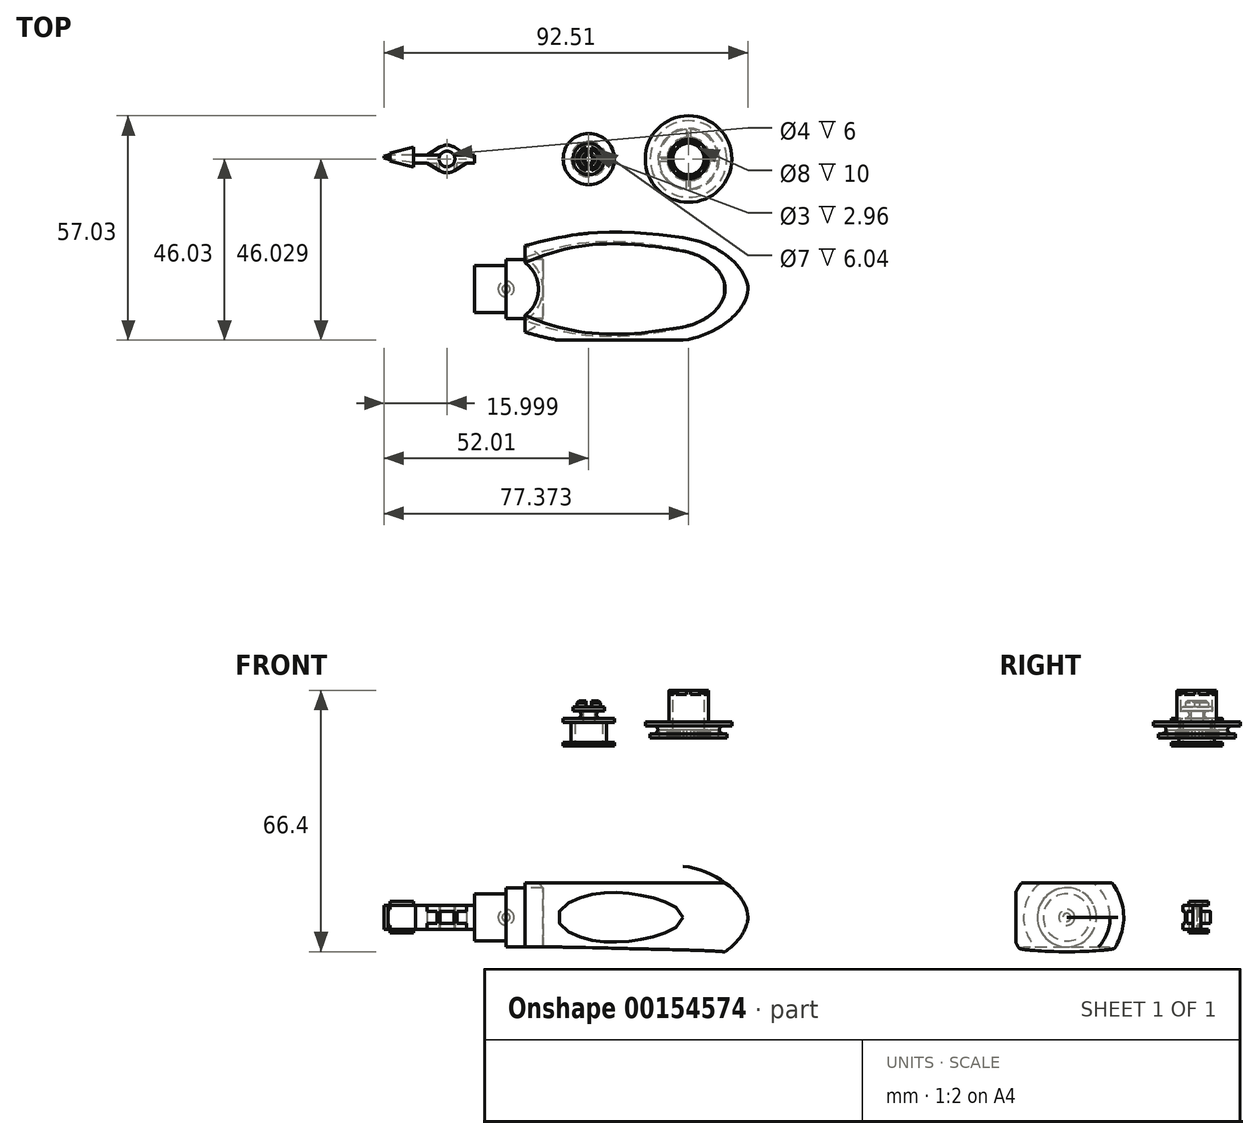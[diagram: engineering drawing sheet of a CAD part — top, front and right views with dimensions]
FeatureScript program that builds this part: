
annotation { "Feature Type Name" : "Feature", "Feature Type Description" : "" }
export const myFeature = defineFeature(function(context is Context, id is Id, definition is map)
    precondition{}
    {
        {
            var Q0;
            Q0=qCreatedBy(makeId("Front.planeOp"),FACE);
            var sketch = newSketch(context, id + "F0", { "sketchPlane" : qUnion([Q0])});
            skLineSegment(sketch, "E0", {"start": v(0, 53.5) * mm, "end": v(1, 53.5) * mm});
            skLineSegment(sketch, "E1", {"start": v(1, 53.5) * mm, "end": v(1, 54.5) * mm});
            skLineSegment(sketch, "E2", {"start": v(1.5, 55) * mm, "end": v(2.5, 55) * mm});
            skLineSegment(sketch, "E3", {"start": v(3, 54.5) * mm, "end": v(3, 53.5) * mm});
            skLineSegment(sketch, "E4", {"start": v(3, 53.5) * mm, "end": v(4, 53.5) * mm});
            skLineSegment(sketch, "E5", {"start": v(4, 53.5) * mm, "end": v(4, 52.5) * mm});
            skLineSegment(sketch, "E6", {"start": v(4, 52.5) * mm, "end": v(3, 52.5) * mm});
            skLineSegment(sketch, "E7", {"start": v(0, 52.5) * mm, "end": v(0, 53.5) * mm});
            skLineSegment(sketch, "E8", {"start": v(3, 50.5) * mm, "end": v(6.5, 50.5) * mm});
            skLineSegment(sketch, "E9", {"start": v(6.5, 50.5) * mm, "end": v(6.5, 49.54) * mm});
            skLineSegment(sketch, "E10", {"start": v(6.5, 49.54) * mm, "end": v(4.5, 49.54) * mm});
            skLineSegment(sketch, "E11", {"start": v(4.5, 49.54) * mm, "end": v(4.5, 44.5) * mm});
            skLineSegment(sketch, "E12", {"start": v(4.5, 44.5) * mm, "end": v(6.5, 44.5) * mm});
            skLineSegment(sketch, "E13", {"start": v(6.5, 44.5) * mm, "end": v(6.5, 43.5) * mm});
            skLineSegment(sketch, "E14", {"start": v(6.5, 43.5) * mm, "end": v(3.5, 43.5) * mm});
            skLineSegment(sketch, "E15", {"start": v(3.5, 43.5) * mm, "end": v(3.5, 49.54) * mm});
            skLineSegment(sketch, "E16", {"start": v(1.5, 52.5) * mm, "end": v(0, 52.5) * mm});
            skArc(sketch, "E17", {"start": v(3, 52.5) * mm, "mid": v(2, 51.5) * mm, "end": v(3, 50.5) * mm});
            skLineSegment(sketch, "E18", {"start": v(1.5, 52.5) * mm, "end": v(1.5, 49.54) * mm});
            skLineSegment(sketch, "E19", {"start": v(1.5, 49.54) * mm, "end": v(3.5, 49.54) * mm});
            skLineSegment(sketch, "E20", {"start": v(1, 54.5) * mm, "end": v(1.5, 55) * mm});
            skLineSegment(sketch, "E21", {"start": v(2.5, 55) * mm, "end": v(3, 54.5) * mm});
            skLineSegment(sketch, "E22", {"start": v(0, 52.5) * mm, "end": v(0, 82.14) * mm, "construction": true});
            skSolve(sketch);
        }
        {
            var Q0;
            Q0 = qSketchRegion(id + "F0", true);
            var Q1;
            Q1=sQuery(id+"F0.wireOp",EDGE,"E22");
            revolve(context, id + "F1", {"entities" : qUnion([Q0]), "axis" : qUnion([Q1]), "revolveType" : RevolveType.FULL});
        }
        {
            var Q0;
            Q0=qCreatedBy(makeId("Front.planeOp"),FACE);
            var sketch = newSketch(context, id + "F2", { "sketchPlane" : qUnion([Q0])});
            skLineSegment(sketch, "E23", {"start": v(0, 53.5) * mm, "end": v(0.75, 53.5) * mm});
            skLineSegment(sketch, "E24", {"start": v(0.75, 53.5) * mm, "end": v(0.75, 55.5) * mm});
            skLineSegment(sketch, "E25", {"start": v(0.75, 55.5) * mm, "end": v(-0.75, 55.5) * mm});
            skLineSegment(sketch, "E26", {"start": v(-0.75, 55.5) * mm, "end": v(-0.75, 53.5) * mm});
            skLineSegment(sketch, "E27", {"start": v(-0.75, 53.5) * mm, "end": v(0, 53.5) * mm});
            skSolve(sketch);
        }
        {
            var Q0;
            Q0 = qSketchRegion(id + "F2", true);
            extrude(context, id + "F3", {"entities" : qUnion([Q0]), "operationType" : NewBodyOperationType.REMOVE, "endBound" : BoundingType.SYMMETRIC, "oppositeDirection" : true, "depth" : 25 * mm});
        }
        {
            var Q0;
            Q0=qCreatedBy(makeId("Front.planeOp"),FACE);
            var sketch = newSketch(context, id + "F4", { "sketchPlane" : qUnion([Q0])});
            skLineSegment(sketch, "E28", {"start": v(25.36, 78.8) * mm, "end": v(25.36, 27.62) * mm, "construction": true});
            skLineSegment(sketch, "E29", {"start": v(29.36, 57.64) * mm, "end": v(30.36, 57.64) * mm});
            skLineSegment(sketch, "E30", {"start": v(30.36, 57.64) * mm, "end": v(30.36, 49.64) * mm});
            skLineSegment(sketch, "E31", {"start": v(30.36, 49.64) * mm, "end": v(36.36, 49.64) * mm});
            skLineSegment(sketch, "E32", {"start": v(36.36, 49.64) * mm, "end": v(36.36, 48.64) * mm});
            skLineSegment(sketch, "E33", {"start": v(36.36, 48.64) * mm, "end": v(34.18, 48.64) * mm});
            skLineSegment(sketch, "E34", {"start": v(34.18, 46.64) * mm, "end": v(35.1, 46.64) * mm});
            skLineSegment(sketch, "E35", {"start": v(35.1, 46.64) * mm, "end": v(35.1, 45.64) * mm});
            skLineSegment(sketch, "E36", {"start": v(35.1, 45.64) * mm, "end": v(29.36, 45.64) * mm});
            skArc(sketch, "E37", {"start": v(34.18, 48.64) * mm, "mid": v(33.18, 47.64) * mm, "end": v(34.18, 46.64) * mm});
            skLineSegment(sketch, "E38", {"start": v(29.36, 57.64) * mm, "end": v(29.36, 45.64) * mm});
            skSolve(sketch);
        }
        {
            var Q0;
            Q0=makeQuery(id+"F4.imprint","IMPRINT",FACE,{"disambiguationData":[TD([[makeQuery(id+"F4.imprint","IMPRINT",EDGE,{"derivedFrom":sQuery(id+"F4.wireOp",EDGE,"E29")}),-1.0]])]});
            var Q1;
            Q1=sQuery(id+"F4.wireOp",EDGE,"E28");
            revolve(context, id + "F5", {"entities" : qUnion([Q0]), "axis" : qUnion([Q1]), "revolveType" : RevolveType.FULL});
        }
        {
            var Q0;
            Q0=makeQuery(id+"F5.opRevolve","SWEPT_FACE",FACE,{"disambiguationData":[OSD([sQuery(id+"F4.wireOp",EDGE,"E36")])]});
            var sketch = newSketch(context, id + "F6", { "sketchPlane" : qUnion([Q0])});
            skArc(sketch, "E39", {"start": v(23.92, 4.79) * mm, "mid": v(23.45, 4.62) * mm, "end": v(23, 4.4) * mm});
            skArc(sketch, "E40", {"start": v(24.86, 5.48) * mm, "mid": v(21.47, 3.89) * mm, "end": v(19.89, 0.5) * mm});
            skArc(sketch, "E41", {"start": v(24.86, 7.48) * mm, "mid": v(20.06, 5.3) * mm, "end": v(17.88, 0.5) * mm});
            skLineSegment(sketch, "E42", {"start": v(17.88, 0.5) * mm, "end": v(19.89, 0.5) * mm});
            skLineSegment(sketch, "E43.MirrorCS", {"start": v(17.88, -0.5) * mm, "end": v(19.89, -0.5) * mm});
            skLineSegment(sketch, "E44", {"start": v(25.36, 0) * mm, "end": v(25.36, 17.53) * mm, "construction": true});
            skLineSegment(sketch, "E45.MirrorCS", {"start": v(32.85, 0.5) * mm, "end": v(30.84, 0.5) * mm});
            skLineSegment(sketch, "E46.MirrorCS", {"start": v(32.85, -0.5) * mm, "end": v(30.84, -0.5) * mm});
            skLineSegment(sketch, "E47", {"start": v(24.86, 7.48) * mm, "end": v(24.86, 5.48) * mm});
            skLineSegment(sketch, "E48.MirrorCS", {"start": v(25.86, 7.48) * mm, "end": v(25.86, 5.48) * mm});
            skLineSegment(sketch, "E49.MirrorCS", {"start": v(24.86, -7.48) * mm, "end": v(24.86, -5.48) * mm});
            skLineSegment(sketch, "E50.MirrorCS", {"start": v(25.86, -7.48) * mm, "end": v(25.86, -5.48) * mm});
            skArc(sketch, "E51.trimOffspring", {"start": v(17.88, -0.5) * mm, "mid": v(20.06, -5.3) * mm, "end": v(24.86, -7.48) * mm});
            skArc(sketch, "E52.trimOffspring", {"start": v(19.89, -0.5) * mm, "mid": v(21.47, -3.89) * mm, "end": v(24.86, -5.48) * mm});
            skArc(sketch, "E53.trimOffspring", {"start": v(25.86, -5.48) * mm, "mid": v(29.25, -3.89) * mm, "end": v(30.84, -0.5) * mm});
            skArc(sketch, "E54.trimOffspring", {"start": v(25.86, -7.48) * mm, "mid": v(30.67, -5.3) * mm, "end": v(32.85, -0.5) * mm});
            skArc(sketch, "E55.trimOffspring", {"start": v(30.84, 0.5) * mm, "mid": v(29.25, 3.89) * mm, "end": v(25.86, 5.48) * mm});
            skArc(sketch, "E56.trimOffspring", {"start": v(32.85, 0.5) * mm, "mid": v(30.67, 5.3) * mm, "end": v(25.86, 7.48) * mm});
            skLineSegment(sketch, "E57", {"start": v(24.86, 4.97) * mm, "end": v(24.86, 4.47) * mm});
            skArc(sketch, "E58", {"start": v(24.86, 4.47) * mm, "mid": v(24.48, 4.41) * mm, "end": v(24.11, 4.32) * mm});
            skLineSegment(sketch, "E59.MirrorCS", {"start": v(25.86, 4.97) * mm, "end": v(25.86, 4.47) * mm});
            skLineSegment(sketch, "E60.1.0", {"start": v(23, 4.4) * mm, "end": v(23.19, 3.94) * mm});
            skLineSegment(sketch, "E60.1.1", {"start": v(23.92, 4.79) * mm, "end": v(24.11, 4.32) * mm});
            skLineSegment(sketch, "E60.2.0", {"start": v(21.5, 3.16) * mm, "end": v(21.85, 2.8) * mm});
            skLineSegment(sketch, "E60.2.1", {"start": v(22.2, 3.87) * mm, "end": v(22.55, 3.52) * mm});
            skLineSegment(sketch, "E60.3.0", {"start": v(20.57, 1.44) * mm, "end": v(21.04, 1.25) * mm});
            skLineSegment(sketch, "E60.3.1", {"start": v(20.96, 2.37) * mm, "end": v(21.42, 2.17) * mm});
            skLineSegment(sketch, "E60.4.0", {"start": v(20.39, -0.5) * mm, "end": v(20.9, -0.5) * mm});
            skLineSegment(sketch, "E60.4.1", {"start": v(20.39, 0.5) * mm, "end": v(20.9, 0.5) * mm});
            skLineSegment(sketch, "E60.5.0", {"start": v(20.96, -2.37) * mm, "end": v(21.42, -2.17) * mm});
            skLineSegment(sketch, "E60.5.1", {"start": v(20.57, -1.44) * mm, "end": v(21.04, -1.25) * mm});
            skLineSegment(sketch, "E60.6.0", {"start": v(22.2, -3.87) * mm, "end": v(22.55, -3.52) * mm});
            skLineSegment(sketch, "E60.6.1", {"start": v(21.5, -3.16) * mm, "end": v(21.85, -2.8) * mm});
            skLineSegment(sketch, "E60.7.0", {"start": v(23.92, -4.79) * mm, "end": v(24.11, -4.32) * mm});
            skLineSegment(sketch, "E60.7.1", {"start": v(23, -4.4) * mm, "end": v(23.19, -3.94) * mm});
            skLineSegment(sketch, "E60.8.0", {"start": v(25.86, -4.97) * mm, "end": v(25.86, -4.47) * mm});
            skLineSegment(sketch, "E60.8.1", {"start": v(24.86, -4.97) * mm, "end": v(24.86, -4.47) * mm});
            skLineSegment(sketch, "E60.9.0", {"start": v(27.73, -4.4) * mm, "end": v(27.54, -3.94) * mm});
            skLineSegment(sketch, "E60.9.1", {"start": v(26.8, -4.79) * mm, "end": v(26.61, -4.32) * mm});
            skLineSegment(sketch, "E60.10.0", {"start": v(29.23, -3.16) * mm, "end": v(28.88, -2.8) * mm});
            skLineSegment(sketch, "E60.10.1", {"start": v(28.53, -3.87) * mm, "end": v(28.17, -3.52) * mm});
            skLineSegment(sketch, "E60.11.0", {"start": v(30.15, -1.44) * mm, "end": v(29.69, -1.25) * mm});
            skLineSegment(sketch, "E60.11.1", {"start": v(29.77, -2.37) * mm, "end": v(29.3, -2.17) * mm});
            skLineSegment(sketch, "E60.12.0", {"start": v(30.34, 0.5) * mm, "end": v(29.83, 0.5) * mm});
            skLineSegment(sketch, "E60.12.1", {"start": v(30.34, -0.5) * mm, "end": v(29.83, -0.5) * mm});
            skLineSegment(sketch, "E60.13.0", {"start": v(29.77, 2.37) * mm, "end": v(29.3, 2.17) * mm});
            skLineSegment(sketch, "E60.13.1", {"start": v(30.15, 1.44) * mm, "end": v(29.69, 1.25) * mm});
            skLineSegment(sketch, "E60.14.0", {"start": v(28.53, 3.87) * mm, "end": v(28.17, 3.52) * mm});
            skLineSegment(sketch, "E60.14.1", {"start": v(29.23, 3.16) * mm, "end": v(28.88, 2.8) * mm});
            skLineSegment(sketch, "E60.15.0", {"start": v(26.8, 4.79) * mm, "end": v(26.61, 4.32) * mm});
            skLineSegment(sketch, "E60.15.1", {"start": v(27.73, 4.4) * mm, "end": v(27.54, 3.94) * mm});
            skArc(sketch, "E61.trimOffspring", {"start": v(26.61, 4.32) * mm, "mid": v(26.24, 4.41) * mm, "end": v(25.86, 4.47) * mm});
            skArc(sketch, "E62.trimOffspring", {"start": v(28.17, 3.52) * mm, "mid": v(27.86, 3.74) * mm, "end": v(27.54, 3.94) * mm});
            skArc(sketch, "E63.trimOffspring", {"start": v(29.3, 2.17) * mm, "mid": v(29.1, 2.5) * mm, "end": v(28.88, 2.8) * mm});
            skArc(sketch, "E64.trimOffspring", {"start": v(29.83, 0.5) * mm, "mid": v(29.78, 0.88) * mm, "end": v(29.69, 1.25) * mm});
            skArc(sketch, "E65.trimOffspring", {"start": v(29.69, -1.25) * mm, "mid": v(29.78, -0.88) * mm, "end": v(29.83, -0.5) * mm});
            skArc(sketch, "E66.trimOffspring", {"start": v(28.88, -2.8) * mm, "mid": v(29.1, -2.5) * mm, "end": v(29.3, -2.17) * mm});
            skArc(sketch, "E67.trimOffspring", {"start": v(27.54, -3.94) * mm, "mid": v(27.86, -3.74) * mm, "end": v(28.17, -3.52) * mm});
            skArc(sketch, "E68.trimOffspring", {"start": v(25.86, -4.47) * mm, "mid": v(26.24, -4.41) * mm, "end": v(26.61, -4.32) * mm});
            skArc(sketch, "E69.trimOffspring", {"start": v(24.11, -4.32) * mm, "mid": v(24.48, -4.41) * mm, "end": v(24.86, -4.47) * mm});
            skArc(sketch, "E70.trimOffspring", {"start": v(22.55, -3.52) * mm, "mid": v(22.86, -3.74) * mm, "end": v(23.19, -3.94) * mm});
            skArc(sketch, "E71.trimOffspring", {"start": v(21.42, -2.17) * mm, "mid": v(21.62, -2.5) * mm, "end": v(21.85, -2.8) * mm});
            skArc(sketch, "E72.trimOffspring", {"start": v(20.9, -0.5) * mm, "mid": v(20.95, -0.88) * mm, "end": v(21.04, -1.25) * mm});
            skArc(sketch, "E73.trimOffspring", {"start": v(21.04, 1.25) * mm, "mid": v(20.95, 0.88) * mm, "end": v(20.9, 0.5) * mm});
            skArc(sketch, "E74.trimOffspring", {"start": v(21.85, 2.8) * mm, "mid": v(21.62, 2.5) * mm, "end": v(21.42, 2.17) * mm});
            skArc(sketch, "E75.trimOffspring", {"start": v(23.19, 3.94) * mm, "mid": v(22.86, 3.74) * mm, "end": v(22.55, 3.52) * mm});
            skArc(sketch, "E76.trimOffspring", {"start": v(25.86, 4.97) * mm, "mid": v(25.36, 5) * mm, "end": v(24.86, 4.97) * mm});
            skArc(sketch, "E77.trimOffspring", {"start": v(27.73, 4.4) * mm, "mid": v(27.28, 4.62) * mm, "end": v(26.8, 4.79) * mm});
            skArc(sketch, "E78.trimOffspring", {"start": v(29.23, 3.16) * mm, "mid": v(28.9, 3.54) * mm, "end": v(28.53, 3.87) * mm});
            skArc(sketch, "E79.trimOffspring", {"start": v(30.15, 1.44) * mm, "mid": v(29.98, 1.91) * mm, "end": v(29.77, 2.37) * mm});
            skArc(sketch, "E80.trimOffspring", {"start": v(30.34, -0.5) * mm, "mid": v(30.36, 0) * mm, "end": v(30.34, 0.5) * mm});
            skArc(sketch, "E81.trimOffspring", {"start": v(29.77, -2.37) * mm, "mid": v(29.98, -1.91) * mm, "end": v(30.15, -1.44) * mm});
            skArc(sketch, "E82.trimOffspring", {"start": v(28.53, -3.87) * mm, "mid": v(28.9, -3.54) * mm, "end": v(29.23, -3.16) * mm});
            skArc(sketch, "E83.trimOffspring", {"start": v(26.8, -4.79) * mm, "mid": v(27.28, -4.62) * mm, "end": v(27.73, -4.4) * mm});
            skArc(sketch, "E84.trimOffspring", {"start": v(24.86, -4.97) * mm, "mid": v(25.36, -5) * mm, "end": v(25.86, -4.97) * mm});
            skArc(sketch, "E85.trimOffspring", {"start": v(23, -4.4) * mm, "mid": v(23.45, -4.62) * mm, "end": v(23.92, -4.79) * mm});
            skArc(sketch, "E86.trimOffspring", {"start": v(21.5, -3.16) * mm, "mid": v(21.83, -3.54) * mm, "end": v(22.2, -3.87) * mm});
            skArc(sketch, "E87.trimOffspring", {"start": v(20.57, -1.44) * mm, "mid": v(20.74, -1.91) * mm, "end": v(20.96, -2.37) * mm});
            skArc(sketch, "E88.trimOffspring", {"start": v(20.39, 0.5) * mm, "mid": v(20.36, 0) * mm, "end": v(20.39, -0.5) * mm});
            skArc(sketch, "E89.trimOffspring", {"start": v(20.96, 2.37) * mm, "mid": v(20.74, 1.91) * mm, "end": v(20.57, 1.44) * mm});
            skArc(sketch, "E90.trimOffspring", {"start": v(22.2, 3.87) * mm, "mid": v(21.83, 3.54) * mm, "end": v(21.5, 3.16) * mm});
            skSolve(sketch);
        }
        {
            var Q0;
            Q0=makeQuery(id+"F6.imprint","IMPRINT",FACE,{"disambiguationData":[TD([[makeQuery(id+"F6.imprint","IMPRINT",EDGE,{"derivedFrom":sQuery(id+"F6.wireOp",EDGE,"E40")}),-1.0]])]});
            var Q1;
            Q1=makeQuery(id+"F6.imprint","IMPRINT",FACE,{"disambiguationData":[TD([[makeQuery(id+"F6.imprint","IMPRINT",EDGE,{"derivedFrom":sQuery(id+"F6.wireOp",EDGE,"E45.MirrorCS")}),-1.0]])]});
            var Q2;
            Q2=makeQuery(id+"F6.imprint","IMPRINT",FACE,{"disambiguationData":[TD([[makeQuery(id+"F6.imprint","IMPRINT",EDGE,{"derivedFrom":sQuery(id+"F6.wireOp",EDGE,"E46.MirrorCS")}),1.0]])]});
            var Q3;
            Q3=makeQuery(id+"F6.imprint","IMPRINT",FACE,{"disambiguationData":[TD([[makeQuery(id+"F6.imprint","IMPRINT",EDGE,{"derivedFrom":sQuery(id+"F6.wireOp",EDGE,"E43.MirrorCS")}),-1.0]])]});
            var Q4;
            Q4=makeQuery(id+"F6.imprint","IMPRINT",FACE,{"disambiguationData":[TD([[makeQuery(id+"F6.imprint","IMPRINT",EDGE,{"derivedFrom":sQuery(id+"F6.wireOp",EDGE,"E39")}),1.0]])]});
            extrude(context, id + "F7", {"entities" : qUnion([Q0, Q1, Q2, Q3, Q4]), "operationType" : NewBodyOperationType.REMOVE, "oppositeDirection" : true, "depth" : 2 * mm});
        }
        {
            var Q0;
            Q0=makeQuery(id+"F5.opRevolve","SWEPT_FACE",FACE,{"disambiguationData":[OSD([sQuery(id+"F4.wireOp",EDGE,"E29")])]});
            var sketch = newSketch(context, id + "F8", { "sketchPlane" : qUnion([Q0])});
            skArc(sketch, "E91", {"start": v(24.86, 4.47) * mm, "mid": v(23.64, 4.16) * mm, "end": v(22.55, 3.52) * mm});
            skLineSegment(sketch, "E92", {"start": v(25.36, 0) * mm, "end": v(25.36, 7.06) * mm, "construction": true});
            skLineSegment(sketch, "E93", {"start": v(24.86, 4.97) * mm, "end": v(24.86, 4.47) * mm});
            skArc(sketch, "E94", {"start": v(25.86, 4.97) * mm, "mid": v(25.36, 5) * mm, "end": v(24.86, 4.97) * mm});
            skLineSegment(sketch, "E95.MirrorCS", {"start": v(25.86, 4.97) * mm, "end": v(25.86, 4.47) * mm});
            skLineSegment(sketch, "E96.1.0", {"start": v(-16.74, 19.04) * mm, "end": v(-16.3, 19.3) * mm});
            skArc(sketch, "E96.1.1", {"start": v(-17.24, 19.91) * mm, "mid": v(-17.01, 19.46) * mm, "end": v(-16.74, 19.04) * mm});
            skLineSegment(sketch, "E96.1.2", {"start": v(-17.24, 19.91) * mm, "end": v(-16.8, 20.16) * mm});
            skLineSegment(sketch, "E96.2.0", {"start": v(-8.12, -24.02) * mm, "end": v(-8.56, -23.77) * mm});
            skArc(sketch, "E96.2.1", {"start": v(-8.62, -24.89) * mm, "mid": v(-8.35, -24.46) * mm, "end": v(-8.12, -24.02) * mm});
            skLineSegment(sketch, "E96.2.2", {"start": v(-8.62, -24.89) * mm, "end": v(-9.06, -24.63) * mm});
            skPoint(sketch, "E96.center", {"position": v(0, 0) * mm});
            skArc(sketch, "E97.1.0", {"start": v(22.2, 3.87) * mm, "mid": v(21.83, 3.54) * mm, "end": v(21.5, 3.16) * mm});
            skLineSegment(sketch, "E97.1.1", {"start": v(21.5, 3.16) * mm, "end": v(21.85, 2.8) * mm});
            skLineSegment(sketch, "E97.1.2", {"start": v(22.2, 3.87) * mm, "end": v(22.55, 3.52) * mm});
            skArc(sketch, "E97.2.0", {"start": v(20.39, 0.5) * mm, "mid": v(20.36, 0) * mm, "end": v(20.39, -0.5) * mm});
            skLineSegment(sketch, "E97.2.1", {"start": v(20.39, -0.5) * mm, "end": v(20.9, -0.5) * mm});
            skLineSegment(sketch, "E97.2.2", {"start": v(20.39, 0.5) * mm, "end": v(20.9, 0.5) * mm});
            skArc(sketch, "E97.3.0", {"start": v(21.5, -3.16) * mm, "mid": v(21.83, -3.54) * mm, "end": v(22.2, -3.87) * mm});
            skLineSegment(sketch, "E97.3.1", {"start": v(22.2, -3.87) * mm, "end": v(22.55, -3.52) * mm});
            skLineSegment(sketch, "E97.3.2", {"start": v(21.5, -3.16) * mm, "end": v(21.85, -2.8) * mm});
            skArc(sketch, "E97.4.0", {"start": v(24.86, -4.97) * mm, "mid": v(25.36, -5) * mm, "end": v(25.86, -4.97) * mm});
            skLineSegment(sketch, "E97.4.1", {"start": v(25.86, -4.97) * mm, "end": v(25.86, -4.47) * mm});
            skLineSegment(sketch, "E97.4.2", {"start": v(24.86, -4.97) * mm, "end": v(24.86, -4.47) * mm});
            skArc(sketch, "E97.5.0", {"start": v(28.53, -3.87) * mm, "mid": v(28.9, -3.54) * mm, "end": v(29.23, -3.16) * mm});
            skLineSegment(sketch, "E97.5.1", {"start": v(29.23, -3.16) * mm, "end": v(28.88, -2.8) * mm});
            skLineSegment(sketch, "E97.5.2", {"start": v(28.53, -3.87) * mm, "end": v(28.17, -3.52) * mm});
            skArc(sketch, "E97.6.0", {"start": v(30.34, -0.5) * mm, "mid": v(30.36, 0) * mm, "end": v(30.34, 0.5) * mm});
            skLineSegment(sketch, "E97.6.1", {"start": v(30.34, 0.5) * mm, "end": v(29.83, 0.5) * mm});
            skLineSegment(sketch, "E97.6.2", {"start": v(30.34, -0.5) * mm, "end": v(29.83, -0.5) * mm});
            skArc(sketch, "E97.7.0", {"start": v(29.23, 3.16) * mm, "mid": v(28.9, 3.54) * mm, "end": v(28.53, 3.87) * mm});
            skLineSegment(sketch, "E97.7.1", {"start": v(28.53, 3.87) * mm, "end": v(28.17, 3.52) * mm});
            skLineSegment(sketch, "E97.7.2", {"start": v(29.23, 3.16) * mm, "end": v(28.88, 2.8) * mm});
            skArc(sketch, "E98.trimOffspring", {"start": v(21.85, 2.8) * mm, "mid": v(21.2, 1.72) * mm, "end": v(20.9, 0.5) * mm});
            skArc(sketch, "E99.trimOffspring", {"start": v(20.9, -0.5) * mm, "mid": v(21.2, -1.72) * mm, "end": v(21.85, -2.8) * mm});
            skArc(sketch, "E100.trimOffspring", {"start": v(22.55, -3.52) * mm, "mid": v(23.64, -4.16) * mm, "end": v(24.86, -4.47) * mm});
            skArc(sketch, "E101.trimOffspring", {"start": v(25.86, -4.47) * mm, "mid": v(27.08, -4.16) * mm, "end": v(28.17, -3.52) * mm});
            skArc(sketch, "E102.trimOffspring", {"start": v(28.88, -2.8) * mm, "mid": v(29.52, -1.72) * mm, "end": v(29.83, -0.5) * mm});
            skArc(sketch, "E103.trimOffspring", {"start": v(29.83, 0.5) * mm, "mid": v(29.52, 1.72) * mm, "end": v(28.88, 2.8) * mm});
            skArc(sketch, "E104.trimOffspring", {"start": v(28.17, 3.52) * mm, "mid": v(27.08, 4.16) * mm, "end": v(25.86, 4.47) * mm});
            skSolve(sketch);
        }
        {
            var Q0;
            Q0=makeQuery(id+"F8.imprint","IMPRINT",FACE,{"disambiguationData":[TD([[makeQuery(id+"F8.imprint","IMPRINT",EDGE,{"derivedFrom":sQuery(id+"F8.wireOp",EDGE,"E91")}),-1.0]])]});
            var Q1;
            {var subQ0=sQuery(id+"F8.wireOp",EDGE,"E95.MirrorCS");Q1=makeQuery(id+"F8.imprint","IMPRINT",FACE,{"disambiguationData":[TD([[makeQuery(id+"F8.imprint","IMPRINT",EDGE,{"derivedFrom":subQ0}),1.0]])]});}
            var Q2;
            {var subQ0=sQuery(id+"F8.wireOp",EDGE,"E97.6.1");Q2=makeQuery(id+"F8.imprint","IMPRINT",FACE,{"disambiguationData":[TD([[makeQuery(id+"F8.imprint","IMPRINT",EDGE,{"derivedFrom":subQ0}),-1.0]])]});}
            var Q3;
            {var subQ0=sQuery(id+"F8.wireOp",EDGE,"E97.5.1");Q3=makeQuery(id+"F8.imprint","IMPRINT",FACE,{"disambiguationData":[TD([[makeQuery(id+"F8.imprint","IMPRINT",EDGE,{"derivedFrom":subQ0}),-1.0]])]});}
            var Q4;
            {var subQ0=sQuery(id+"F8.wireOp",EDGE,"E97.4.1");Q4=makeQuery(id+"F8.imprint","IMPRINT",FACE,{"disambiguationData":[TD([[makeQuery(id+"F8.imprint","IMPRINT",EDGE,{"derivedFrom":subQ0}),-1.0]])]});}
            var Q5;
            {var subQ0=sQuery(id+"F8.wireOp",EDGE,"E97.3.1");Q5=makeQuery(id+"F8.imprint","IMPRINT",FACE,{"disambiguationData":[TD([[makeQuery(id+"F8.imprint","IMPRINT",EDGE,{"derivedFrom":subQ0}),-1.0]])]});}
            var Q6;
            {var subQ0=sQuery(id+"F8.wireOp",EDGE,"E97.2.1");Q6=makeQuery(id+"F8.imprint","IMPRINT",FACE,{"disambiguationData":[TD([[makeQuery(id+"F8.imprint","IMPRINT",EDGE,{"derivedFrom":subQ0}),-1.0]])]});}
            var Q7;
            {var subQ0=sQuery(id+"F8.wireOp",EDGE,"E97.1.1");Q7=makeQuery(id+"F8.imprint","IMPRINT",FACE,{"disambiguationData":[TD([[makeQuery(id+"F8.imprint","IMPRINT",EDGE,{"derivedFrom":subQ0}),-1.0]])]});}
            extrude(context, id + "F9", {"entities" : qUnion([Q0, Q1, Q2, Q3, Q4, Q5, Q6, Q7]), "operationType" : NewBodyOperationType.REMOVE, "oppositeDirection" : true, "depth" : 1 * mm});
        }
        {
            var Q0;
            Q0=qCreatedBy(makeId("Top.planeOp"),FACE);
            var sketch = newSketch(context, id + "F10", { "sketchPlane" : qUnion([Q0])});
            skLineSegment(sketch, "E105", {"start": v(-66.73, 0) * mm, "end": v(-11.16, 0) * mm, "construction": true});
            skLineSegment(sketch, "E106", {"start": v(-52.01, 0.25) * mm, "end": v(-52.01, 0.75) * mm});
            skLineSegment(sketch, "E107", {"start": v(-29.01, 1) * mm, "end": v(-29.01, -1) * mm});
            skLineSegment(sketch, "E108", {"start": v(-36.01, -3.5) * mm, "end": v(-36.01, -3.5) * mm});
            skCircle(sketch, "E109", {"center": v(-36.01, 0) * mm, "radius": 2 * mm});
            skLineSegment(sketch, "E110.top", {"start": v(-29.01, 1) * mm, "end": v(-31.01, 1) * mm});
            skLineSegment(sketch, "E111", {"start": v(-31.01, 1) * mm, "end": v(-34.16, 2.97) * mm});
            skLineSegment(sketch, "E112.MirrorCS", {"start": v(-31.01, -1) * mm, "end": v(-34.16, -2.97) * mm});
            skLineSegment(sketch, "E113.MirrorCS", {"start": v(-29.01, -1) * mm, "end": v(-31.01, -1) * mm});
            skLineSegment(sketch, "E114.MirrorCS", {"start": v(-41.01, 1) * mm, "end": v(-37.87, 2.97) * mm});
            skLineSegment(sketch, "E115.MirrorCS", {"start": v(-41.01, -1) * mm, "end": v(-37.87, -2.97) * mm});
            skLineSegment(sketch, "E116", {"start": v(-31.01, 1) * mm, "end": v(-34.28, 1) * mm});
            skLineSegment(sketch, "E117", {"start": v(-41.01, -1) * mm, "end": v(-44.01, -1) * mm});
            skLineSegment(sketch, "E118", {"start": v(-44.01, -1) * mm, "end": v(-51.01, 0) * mm});
            skLineSegment(sketch, "E119", {"start": v(-51.01, 0) * mm, "end": v(-52.01, 0.25) * mm});
            skLineSegment(sketch, "E120", {"start": v(-51.01, 1) * mm, "end": v(-52.01, 0.75) * mm});
            skLineSegment(sketch, "E121.trimOffspring", {"start": v(-37.74, 1) * mm, "end": v(-51.01, 1) * mm});
            skArc(sketch, "E122.trimOffspring", {"start": v(-34.16, 2.97) * mm, "mid": v(-36.01, 3.5) * mm, "end": v(-37.87, 2.97) * mm});
            skArc(sketch, "E123.trimOffspring", {"start": v(-37.87, -2.97) * mm, "mid": v(-36.01, -3.5) * mm, "end": v(-34.16, -2.97) * mm});
            skLineSegment(sketch, "E124", {"start": v(-50.51, 1.5) * mm, "end": v(-50.51, 0.5) * mm});
            skLineSegment(sketch, "E125.MirrorCS", {"start": v(-50.51, -0.5) * mm, "end": v(-50.51, 0.5) * mm});
            skLineSegment(sketch, "E126", {"start": v(-44.37, 0.5) * mm, "end": v(-44.37, 3) * mm});
            skLineSegment(sketch, "E127", {"start": v(-50.51, 1.5) * mm, "end": v(-44.37, 3) * mm});
            skLineSegment(sketch, "E128.MirrorCS", {"start": v(-44.37, 0.5) * mm, "end": v(-44.37, -2) * mm});
            skLineSegment(sketch, "E129.MirrorCS", {"start": v(-50.51, -0.5) * mm, "end": v(-44.37, -2) * mm});
            skLineSegment(sketch, "E130", {"start": v(-51.01, 1) * mm, "end": v(-51.01, 0) * mm});
            skSolve(sketch);
        }
        {
            var Q0;
            Q0=makeQuery(id+"F10.imprint","IMPRINT",FACE,{"disambiguationData":[TD([[makeQuery(id+"F10.imprint","IMPRINT",EDGE,{"derivedFrom":sQuery(id+"F10.wireOp",EDGE,"E111")}),1.0]])]});
            var Q1;
            Q1=makeQuery(id+"F10.imprint","IMPRINT",FACE,{"disambiguationData":[TD([[makeQuery(id+"F10.imprint","IMPRINT",EDGE,{"derivedFrom":sQuery(id+"F10.wireOp",EDGE,"E107")}),-1.0]])]});
            var Q2;
            {var subQ3=sQuery(id+"F10.wireOp",EDGE,"E118");var subQ5=sQuery(id+"F10.wireOp",EDGE,"E128.MirrorCS");var subQ11=makeQuery(id+"F10.imprint","INTERSECT",VERTEX,{"derivedFrom":[subQ3,subQ5]});Q2=makeQuery(id+"F10.imprint","IMPRINT",FACE,{"disambiguationData":[TD([[makeQuery(id+"F10.imprint","IMPRINT",EDGE,{"disambiguationData":[TD([[subQ11,-1.0]])],"derivedFrom":subQ3}),-1.0]])]});}
            var Q3;
            {var subQ7=sQuery(id+"F10.wireOp",EDGE,"E130");Q3=makeQuery(id+"F10.imprint","IMPRINT",FACE,{"disambiguationData":[TD([[makeQuery(id+"F10.imprint","IMPRINT",EDGE,{"derivedFrom":subQ7}),1.0]])]});}
            var Q4;
            Q4=makeQuery(id+"F10.imprint","IMPRINT",FACE,{"disambiguationData":[TD([[makeQuery(id+"F10.imprint","IMPRINT",EDGE,{"derivedFrom":sQuery(id+"F10.wireOp",EDGE,"E106")}),-1.0]])]});
            extrude(context, id + "F11", {"entities" : qUnion([Q0, Q1, Q2, Q3, Q4]), "endBound" : BoundingType.SYMMETRIC, "depth" : 6 * mm});
        }
        {
            var Q0;
            {var subQ0=sQuery(id+"F10.wireOp",EDGE,"E121.trimOffspring");Q0=makeQuery(id+"F11.opExtrude","SWEPT_FACE",FACE,{"disambiguationData":[OSD([subQ0]),TDD([makeQuery(id+"F10.imprint","IMPRINT",EDGE,{"disambiguationData":[TD([[makeQuery(id+"F10.imprint","INTERSECT",VERTEX,{"derivedFrom":[sQuery(id+"F10.wireOp",EDGE,"E114.MirrorCS"),subQ0]}),-1.0]])],"derivedFrom":subQ0})])]});}
            var sketch = newSketch(context, id + "F12", { "sketchPlane" : qUnion([Q0])});
            skLineSegment(sketch, "E131", {"start": v(41.01, -3) * mm, "end": v(41.01, -1.5) * mm});
            skLineSegment(sketch, "E132", {"start": v(41.01, -1.5) * mm, "end": v(31.01, -1.5) * mm});
            skLineSegment(sketch, "E133", {"start": v(31.01, -1.5) * mm, "end": v(31.01, -3) * mm});
            skLineSegment(sketch, "E134", {"start": v(41.01, -3) * mm, "end": v(31.01, -3) * mm});
            skLineSegment(sketch, "E135.MirrorCS", {"start": v(31.01, 1.5) * mm, "end": v(31.01, 3) * mm});
            skLineSegment(sketch, "E136.MirrorCS", {"start": v(41.01, 1.5) * mm, "end": v(31.01, 1.5) * mm});
            skLineSegment(sketch, "E137.MirrorCS", {"start": v(41.01, 3) * mm, "end": v(41.01, 1.5) * mm});
            skLineSegment(sketch, "E138.MirrorCS", {"start": v(41.01, 3) * mm, "end": v(31.01, 3) * mm});
            skSolve(sketch);
        }
        {
            var Q0;
            Q0 = qSketchRegion(id + "F12", true);
            extrude(context, id + "F13", {"entities" : qUnion([Q0]), "operationType" : NewBodyOperationType.REMOVE, "endBound" : BoundingType.THROUGH_ALL, "depth" : 8.08 * mm});
        }
        {
            var Q0;
            Q0=makeQuery(id+"F13.boolean.opBoolean","MERGE",FACE,{"derivedFrom":[makeQuery(id+"F11.opExtrude","SWEPT_FACE",FACE,{"disambiguationData":[OSD([sQuery(id+"F10.wireOp",EDGE,"E121.trimOffspring")])]}),makeQuery(id+"F13.opExtrude","CAP_FACE",FACE,{"disambiguationData":[OSD([sQuery(id+"F12.wireOp",EDGE,"E131"),sQuery(id+"F12.wireOp",EDGE,"E132"),sQuery(id+"F12.wireOp",EDGE,"E133"),sQuery(id+"F12.wireOp",EDGE,"E134")])],"isStart":true}),makeQuery(id+"F13.opExtrude","CAP_FACE",FACE,{"disambiguationData":[OSD([sQuery(id+"F12.wireOp",EDGE,"E135.MirrorCS"),sQuery(id+"F12.wireOp",EDGE,"E136.MirrorCS"),sQuery(id+"F12.wireOp",EDGE,"E137.MirrorCS"),sQuery(id+"F12.wireOp",EDGE,"E138.MirrorCS")])],"isStart":true})]});
            var sketch = newSketch(context, id + "F14", { "sketchPlane" : qUnion([Q0])});
            skLineSegment(sketch, "E139.bottom", {"start": v(51.01, -3) * mm, "end": v(50.51, -3) * mm});
            skLineSegment(sketch, "E139.top", {"start": v(51.01, -2) * mm, "end": v(50.51, -2) * mm});
            skLineSegment(sketch, "E139.left", {"start": v(51.01, -3) * mm, "end": v(51.01, -2) * mm});
            skLineSegment(sketch, "E139.right", {"start": v(50.51, -3) * mm, "end": v(50.51, -2) * mm});
            skLineSegment(sketch, "E140.MirrorCS", {"start": v(51.01, 2) * mm, "end": v(50.51, 2) * mm});
            skLineSegment(sketch, "E141.MirrorCS", {"start": v(50.51, 3) * mm, "end": v(50.51, 2) * mm});
            skLineSegment(sketch, "E142.MirrorCS", {"start": v(51.01, 3) * mm, "end": v(50.51, 3) * mm});
            skLineSegment(sketch, "E143.MirrorCS", {"start": v(51.01, 3) * mm, "end": v(51.01, 2) * mm});
            skSolve(sketch);
        }
        {
            var Q0;
            Q0 = qSketchRegion(id + "F14", true);
            extrude(context, id + "F15", {"entities" : qUnion([Q0]), "operationType" : NewBodyOperationType.REMOVE, "endBound" : BoundingType.THROUGH_ALL, "oppositeDirection" : true, "depth" : 25 * mm});
        }
        {
            var Q0;
            {var subQ0=sQuery(id+"F10.wireOp",EDGE,"E121.trimOffspring");var subQ1=sQuery(id+"F10.wireOp",EDGE,"E118");var subQ2=sQuery(id+"F10.wireOp",EDGE,"E117");var subQ3=sQuery(id+"F10.wireOp",EDGE,"E115.MirrorCS");var subQ4=sQuery(id+"F10.wireOp",EDGE,"E110.top");var subQ5=sQuery(id+"F10.wireOp",EDGE,"E123.trimOffspring");var subQ6=sQuery(id+"F10.wireOp",EDGE,"E113.MirrorCS");var subQ7=sQuery(id+"F10.wireOp",EDGE,"E112.MirrorCS");var subQ8=sQuery(id+"F10.wireOp",EDGE,"E107");var subQ9=sQuery(id+"F10.wireOp",EDGE,"E109");Q0=makeQuery(id+"F15.boolean.opBoolean","SPLIT",FACE,{"disambiguationData":[TD([makeQuery(id+"F11.opExtrude","SWEPT_FACE",FACE,{"disambiguationData":[OSD([subQ8])]})])],"derivedFrom":makeQuery(id+"F11.opExtrude","CAP_FACE",FACE,{"disambiguationData":[OSD([sQuery(id+"F10.wireOp",EDGE,"E106"),subQ8,subQ9,subQ4,sQuery(id+"F10.wireOp",EDGE,"E111"),subQ7,subQ6,sQuery(id+"F10.wireOp",EDGE,"E114.MirrorCS"),subQ3,subQ2,subQ1,sQuery(id+"F10.wireOp",EDGE,"E119"),sQuery(id+"F10.wireOp",EDGE,"E120"),subQ0,sQuery(id+"F10.wireOp",EDGE,"E122.trimOffspring"),subQ5])],"isStart":false})});}
            var sketch = newSketch(context, id + "F16", { "sketchPlane" : qUnion([Q0])});
            skLineSegment(sketch, "E144", {"start": v(-50.51, 0.46) * mm, "end": v(-44.51, 0.46) * mm});
            skLineSegment(sketch, "E145", {"start": v(-50.51, 0.46) * mm, "end": v(-50.51, 1.46) * mm});
            skLineSegment(sketch, "E146", {"start": v(-44.51, 0.46) * mm, "end": v(-44.51, 2.96) * mm});
            skLineSegment(sketch, "E147", {"start": v(-50.51, 1.46) * mm, "end": v(-44.51, 2.96) * mm});
            skLineSegment(sketch, "E148.MirrorCS", {"start": v(-50.51, 0.46) * mm, "end": v(-50.51, -0.54) * mm});
            skLineSegment(sketch, "E149.MirrorCS", {"start": v(-50.51, -0.54) * mm, "end": v(-44.51, -2.04) * mm});
            skLineSegment(sketch, "E150.MirrorCS", {"start": v(-44.51, 0.46) * mm, "end": v(-44.51, -2.04) * mm});
            skSolve(sketch);
        }
        {
            var Q0;
            {var subQ3=sQuery(id+"F16.wireOp",EDGE,"E149.MirrorCS");Q0=makeQuery(id+"F16.imprint","IMPRINT",FACE,{"disambiguationData":[TD([[makeQuery(id+"F16.imprint","IMPRINT",EDGE,{"derivedFrom":subQ3}),1.0]])]});}
            var Q1;
            {var subQ0=sQuery(id+"F16.wireOp",EDGE,"E144");Q1=makeQuery(id+"F16.imprint","IMPRINT",FACE,{"disambiguationData":[TD([[makeQuery(id+"F16.imprint","IMPRINT",EDGE,{"derivedFrom":subQ0}),-1.0]])]});}
            var Q2;
            {var subQ0=sQuery(id+"F16.wireOp",EDGE,"E144");Q2=makeQuery(id+"F16.imprint","IMPRINT",FACE,{"disambiguationData":[TD([[makeQuery(id+"F16.imprint","IMPRINT",EDGE,{"derivedFrom":subQ0}),1.0]])]});}
            var Q3;
            {var subQ3=sQuery(id+"F16.wireOp",EDGE,"E147");Q3=makeQuery(id+"F16.imprint","IMPRINT",FACE,{"disambiguationData":[TD([[makeQuery(id+"F16.imprint","IMPRINT",EDGE,{"derivedFrom":subQ3}),-1.0]])]});}
            extrude(context, id + "F17", {"entities" : qUnion([Q0, Q1, Q2, Q3]), "depth" : 1 * mm});
        }
        {
            var Q0;
            Q0=makeQuery(id+"F17.opExtrude","SWEPT_BODY",BODY,{"disambiguationData":[OSD([sQuery(id+"F16.wireOp",EDGE,"E145"),sQuery(id+"F16.wireOp",EDGE,"E146"),sQuery(id+"F16.wireOp",EDGE,"E147"),sQuery(id+"F16.wireOp",EDGE,"E148.MirrorCS"),sQuery(id+"F16.wireOp",EDGE,"E149.MirrorCS"),sQuery(id+"F16.wireOp",EDGE,"E150.MirrorCS")])]});
            var Q1;
            Q1=qCreatedBy(makeId("Top.planeOp"),FACE);
            mirror(context, id + "F18", {"operationType" : NewBodyOperationType.ADD, "entities" : qUnion([Q0]), "mirrorPlane" : qUnion([Q1])});
        }
        {
            var Q0;
            Q0=makeQuery(id+"F11.opExtrude","SWEPT_FACE",FACE,{"disambiguationData":[OSD([sQuery(id+"F10.wireOp",EDGE,"E113.MirrorCS")])]});
            var sketch = newSketch(context, id + "F19", { "sketchPlane" : qUnion([Q0])});
            skLineSegment(sketch, "E151", {"start": v(-29.01, 0) * mm, "end": v(-41.01, 0) * mm, "construction": true});
            skPoint(sketch, "E151.endSnap0", {"position": v(-29.01, 0) * mm});
            skLineSegment(sketch, "E152", {"start": v(-31.01, 0) * mm, "end": v(-31.01, 1.5) * mm});
            skLineSegment(sketch, "E153", {"start": v(-31.01, 1.5) * mm, "end": v(-33.51, 1.5) * mm});
            skLineSegment(sketch, "E154", {"start": v(-33.51, 1.5) * mm, "end": v(-33.51, 0) * mm});
            skLineSegment(sketch, "E155", {"start": v(-34.16, 0) * mm, "end": v(-34.16, 1.5) * mm});
            skLineSegment(sketch, "E156", {"start": v(-34.16, 1.5) * mm, "end": v(-37.87, 1.5) * mm});
            skLineSegment(sketch, "E157", {"start": v(-37.87, 1.5) * mm, "end": v(-37.87, 0) * mm});
            skLineSegment(sketch, "E158", {"start": v(-41.01, 0) * mm, "end": v(-41.01, 1.5) * mm});
            skLineSegment(sketch, "E159", {"start": v(-41.01, 1.5) * mm, "end": v(-38.51, 1.5) * mm});
            skLineSegment(sketch, "E160", {"start": v(-38.51, 1.5) * mm, "end": v(-38.51, 0) * mm});
            skPoint(sketch, "E161.orphan", {"position": v(-54.6, 0) * mm});
            skLineSegment(sketch, "E162.MirrorCS", {"start": v(-31.01, 0) * mm, "end": v(-31.01, -1.5) * mm});
            skLineSegment(sketch, "E163.MirrorCS", {"start": v(-31.01, -1.5) * mm, "end": v(-33.51, -1.5) * mm});
            skLineSegment(sketch, "E164.MirrorCS", {"start": v(-33.51, -1.5) * mm, "end": v(-33.51, 0) * mm});
            skLineSegment(sketch, "E165.MirrorCS", {"start": v(-34.16, 0) * mm, "end": v(-34.16, -1.5) * mm});
            skLineSegment(sketch, "E166.MirrorCS", {"start": v(-34.16, -1.5) * mm, "end": v(-37.87, -1.5) * mm});
            skLineSegment(sketch, "E167.MirrorCS", {"start": v(-37.87, -1.5) * mm, "end": v(-37.87, 0) * mm});
            skLineSegment(sketch, "E168.MirrorCS", {"start": v(-38.51, -1.5) * mm, "end": v(-38.51, 0) * mm});
            skLineSegment(sketch, "E169.MirrorCS", {"start": v(-41.01, -1.5) * mm, "end": v(-38.51, -1.5) * mm});
            skLineSegment(sketch, "E170.MirrorCS", {"start": v(-41.01, 0) * mm, "end": v(-41.01, -1.5) * mm});
            skSolve(sketch);
        }
        {
            var Q0;
            Q0 = qSketchRegion(id + "F19", true);
            extrude(context, id + "F20", {"entities" : qUnion([Q0]), "operationType" : NewBodyOperationType.REMOVE, "endBound" : BoundingType.THROUGH_ALL, "depth" : 25 * mm});
        }
        {
            var Q0;
            Q0=qCreatedBy(makeId("Top.planeOp"),FACE);
            var sketch = newSketch(context, id + "F21", { "sketchPlane" : qUnion([Q0])});
            skLineSegment(sketch, "E171", {"start": v(-29, -33.03) * mm, "end": v(40.5, -33.03) * mm, "construction": true});
            skLineSegment(sketch, "E172", {"start": v(-29, -33.03) * mm, "end": v(-29, -27.03) * mm});
            skLineSegment(sketch, "E173", {"start": v(-29, -27.03) * mm, "end": v(-21, -27.03) * mm});
            skLineSegment(sketch, "E174", {"start": v(-21, -27.03) * mm, "end": v(-21, -25.53) * mm});
            skLineSegment(sketch, "E175", {"start": v(-21, -25.53) * mm, "end": v(-8.04, -25.53) * mm});
            skLineSegment(sketch, "E176", {"start": v(-21, -27.03) * mm, "end": v(-21, -36.35) * mm, "construction": true});
            skCircle(sketch, "E177", {"center": v(-21, -33.03) * mm, "radius": 2 * mm});
            skCircle(sketch, "E178", {"center": v(-21, -33.03) * mm, "radius": 1 * mm});
            skArc(sketch, "E179", {"start": v(-16.2, -44.03) * mm, "mid": v(-9, -33.03) * mm, "end": v(-16.2, -22.03) * mm});
            skLineSegment(sketch, "E180", {"start": v(0, -33.03) * mm, "end": v(0, -22.03) * mm});
            skLineSegment(sketch, "E181", {"start": v(0, -22.03) * mm, "end": v(-16.2, -22.03) * mm});
            skCircle(sketch, "E182", {"center": v(0, -33.03) * mm, "radius": 3.5 * mm});
            skCircle(sketch, "E183", {"center": v(0, -33.03) * mm, "radius": 2.5 * mm});
            skCircle(sketch, "E184", {"center": v(21, -33.03) * mm, "radius": 4 * mm});
            skCircle(sketch, "E185", {"center": v(21, -33.03) * mm, "radius": 3 * mm});
            skLineSegment(sketch, "E186", {"start": v(-7.89, -46.03) * mm, "end": v(24, -46.03) * mm});
            skLineSegment(sketch, "E187.MirrorCS", {"start": v(-21, -40.53) * mm, "end": v(-8.04, -40.53) * mm});
            skLineSegment(sketch, "E188.MirrorCS", {"start": v(-21, -39.03) * mm, "end": v(-21, -40.53) * mm});
            skLineSegment(sketch, "E189.MirrorCS", {"start": v(-29, -39.03) * mm, "end": v(-21, -39.03) * mm});
            skLineSegment(sketch, "E190.MirrorCS", {"start": v(-29, -33.03) * mm, "end": v(-29, -39.03) * mm});
            skFitSpline(sketch, "E191", {"points": [v(24, -20.03) * mm, v(40.5, -33.03) * mm], "startDerivative": vector(24.72, -3.37) * mm, "endDerivative": vector(1.47, -18.45) * mm});
            skFitSpline(sketch, "E192.MirrorCS", {"points": [v(24, -46.03) * mm, v(40.5, -33.03) * mm], "startDerivative": vector(24.72, 3.37) * mm, "endDerivative": vector(1.47, 18.45) * mm});
            skFitSpline(sketch, "E193", {"points": [v(-16.2, -22.03) * mm, v(24, -20.03) * mm], "startDerivative": vector(41.65, 11.26) * mm, "endDerivative": vector(54.57, -7.43) * mm});
            skFitSpline(sketch, "E194.MirrorCS", {"points": [v(-16.2, -44.03) * mm, v(24, -46.03) * mm], "startDerivative": vector(41.65, -11.26) * mm, "endDerivative": vector(54.57, 7.43) * mm});
            skPoint(sketch, "E195.orphan", {"position": v(-9, -33.03) * mm});
            skPoint(sketch, "E196.MirrorCS.start.orphan", {"position": v(0, -44.03) * mm});
            skLineSegment(sketch, "E197", {"start": v(-8.04, -25.53) * mm, "end": v(-8.04, -40.53) * mm});
            skLineSegment(sketch, "E198", {"start": v(-29, -33.03) * mm, "end": v(-8.04, -33.03) * mm});
            skLineSegment(sketch, "E199", {"start": v(-9, -33.03) * mm, "end": v(40.5, -33.03) * mm});
            skLineSegment(sketch, "E200", {"start": v(-7.89, -46.03) * mm, "end": v(-7.89, -53.84) * mm});
            skLineSegment(sketch, "E201", {"start": v(-7.89, -53.84) * mm, "end": v(24, -53.84) * mm});
            skLineSegment(sketch, "E202", {"start": v(24, -53.84) * mm, "end": v(24, -46.03) * mm});
            skSolve(sketch);
        }
        {
            var Q0;
            {var subQ6=sQuery(id+"F21.wireOp",EDGE,"E172");Q0=makeQuery(id+"F21.imprint","IMPRINT",FACE,{"disambiguationData":[TD([[makeQuery(id+"F21.imprint","IMPRINT",EDGE,{"derivedFrom":subQ6}),-1.0]])]});}
            var Q1;
            {var subQ0=sQuery(id+"F21.wireOp",EDGE,"E197");var subQ1=sQuery(id+"F21.wireOp",EDGE,"E175");var subQ2=makeQuery(id+"F21.imprint","INTERSECT",VERTEX,{"derivedFrom":[subQ1,subQ0]});Q1=makeQuery(id+"F21.imprint","IMPRINT",FACE,{"disambiguationData":[TD([[makeQuery(id+"F21.imprint","IMPRINT",EDGE,{"disambiguationData":[TD([[subQ2,1.0]])],"derivedFrom":subQ1}),-1.0]])]});}
            var Q2;
            {var subQ0=sQuery(id+"F21.wireOp",EDGE,"E198");var subQ1=sQuery(id+"F21.wireOp",EDGE,"E177");var subQ2=makeQuery(id+"F21.imprint","INTERSECT",VERTEX,{"disambiguationData":[OD(0.0)],"derivedFrom":[subQ1,subQ0]});Q2=makeQuery(id+"F21.imprint","IMPRINT",FACE,{"disambiguationData":[TD([[makeQuery(id+"F21.imprint","IMPRINT",EDGE,{"disambiguationData":[TD([[subQ2,1.0]])],"derivedFrom":subQ1}),1.0]])]});}
            var Q3;
            {var subQ0=sQuery(id+"F21.wireOp",EDGE,"E198");var subQ1=sQuery(id+"F21.wireOp",EDGE,"E178");var subQ2=makeQuery(id+"F21.imprint","INTERSECT",VERTEX,{"disambiguationData":[OD(0.0)],"derivedFrom":[subQ1,subQ0]});Q3=makeQuery(id+"F21.imprint","IMPRINT",FACE,{"disambiguationData":[TD([[makeQuery(id+"F21.imprint","IMPRINT",EDGE,{"disambiguationData":[TD([[subQ2,1.0]])],"derivedFrom":subQ1}),1.0]])]});}
            var Q4;
            Q4=sQuery(id+"F21.wireOp",EDGE,"E171");
            revolve(context, id + "F22", {"entities" : qUnion([Q0, Q1, Q2, Q3]), "axis" : qUnion([Q4]), "revolveType" : RevolveType.FULL});
        }
        {
            var Q0;
            {var subQ0=sQuery(id+"F21.wireOp",EDGE,"E181");Q0=makeQuery(id+"F21.imprint","IMPRINT",FACE,{"disambiguationData":[TD([[makeQuery(id+"F21.imprint","IMPRINT",EDGE,{"derivedFrom":subQ0}),1.0]])]});}
            var Q1;
            {var subQ8=sQuery(id+"F21.wireOp",EDGE,"E181");Q1=makeQuery(id+"F21.imprint","IMPRINT",FACE,{"disambiguationData":[TD([[makeQuery(id+"F21.imprint","IMPRINT",EDGE,{"derivedFrom":subQ8}),-1.0]])]});}
            var Q2;
            {var subQ0=sQuery(id+"F21.wireOp",EDGE,"E183");var subQ1=sQuery(id+"F21.wireOp",EDGE,"E180");var subQ2=makeQuery(id+"F21.imprint","INTERSECT",VERTEX,{"derivedFrom":[subQ1,subQ0]});Q2=makeQuery(id+"F21.imprint","IMPRINT",FACE,{"disambiguationData":[TD([[makeQuery(id+"F21.imprint","IMPRINT",EDGE,{"disambiguationData":[TD([[subQ2,-1.0]])],"derivedFrom":subQ1}),1.0]])]});}
            var Q3;
            {var subQ0=sQuery(id+"F21.wireOp",EDGE,"E199");var subQ1=sQuery(id+"F21.wireOp",EDGE,"E180");var subQ2=makeQuery(id+"F21.imprint","INTERSECT",VERTEX,{"derivedFrom":[subQ1,subQ0]});Q3=makeQuery(id+"F21.imprint","IMPRINT",FACE,{"disambiguationData":[TD([[makeQuery(id+"F21.imprint","IMPRINT",EDGE,{"disambiguationData":[TD([[subQ2,-1.0]])],"derivedFrom":subQ1}),1.0]])]});}
            var Q4;
            {var subQ0=sQuery(id+"F21.wireOp",EDGE,"E183");var subQ1=sQuery(id+"F21.wireOp",EDGE,"E180");var subQ2=makeQuery(id+"F21.imprint","INTERSECT",VERTEX,{"derivedFrom":[subQ1,subQ0]});Q4=makeQuery(id+"F21.imprint","IMPRINT",FACE,{"disambiguationData":[TD([[makeQuery(id+"F21.imprint","IMPRINT",EDGE,{"disambiguationData":[TD([[subQ2,-1.0]])],"derivedFrom":subQ1}),-1.0]])]});}
            var Q5;
            {var subQ0=sQuery(id+"F21.wireOp",EDGE,"E199");var subQ1=sQuery(id+"F21.wireOp",EDGE,"E180");var subQ2=makeQuery(id+"F21.imprint","INTERSECT",VERTEX,{"derivedFrom":[subQ1,subQ0]});Q5=makeQuery(id+"F21.imprint","IMPRINT",FACE,{"disambiguationData":[TD([[makeQuery(id+"F21.imprint","IMPRINT",EDGE,{"disambiguationData":[TD([[subQ2,-1.0]])],"derivedFrom":subQ1}),-1.0]])]});}
            var Q6;
            {var subQ0=sQuery(id+"F21.wireOp",EDGE,"E199");var subQ1=sQuery(id+"F21.wireOp",EDGE,"E184");var subQ2=makeQuery(id+"F21.imprint","INTERSECT",VERTEX,{"disambiguationData":[OD(0.0)],"derivedFrom":[subQ1,subQ0]});Q6=makeQuery(id+"F21.imprint","IMPRINT",FACE,{"disambiguationData":[TD([[makeQuery(id+"F21.imprint","IMPRINT",EDGE,{"disambiguationData":[TD([[subQ2,1.0]])],"derivedFrom":subQ1}),1.0]])]});}
            var Q7;
            {var subQ0=sQuery(id+"F21.wireOp",EDGE,"E199");var subQ1=sQuery(id+"F21.wireOp",EDGE,"E185");var subQ2=makeQuery(id+"F21.imprint","INTERSECT",VERTEX,{"disambiguationData":[OD(0.0)],"derivedFrom":[subQ1,subQ0]});Q7=makeQuery(id+"F21.imprint","IMPRINT",FACE,{"disambiguationData":[TD([[makeQuery(id+"F21.imprint","IMPRINT",EDGE,{"disambiguationData":[TD([[subQ2,1.0]])],"derivedFrom":subQ1}),1.0]])]});}
            var Q8;
            Q8=sQuery(id+"F21.wireOp",EDGE,"E199");
            revolve(context, id + "F23", {"operationType" : NewBodyOperationType.ADD, "entities" : qUnion([Q0, Q1, Q2, Q3, Q4, Q5, Q6, Q7]), "axis" : qUnion([Q8]), "revolveType" : RevolveType.FULL});
        }
        {
            var Q0;
            Q0=qCreatedBy(makeId("Front.planeOp"),FACE);
            var sketch = newSketch(context, id + "F24", { "sketchPlane" : qUnion([Q0])});
            skLineSegment(sketch, "E203", {"start": v(-67.55, 0) * mm, "end": v(65.89, 0) * mm, "construction": true});
            skLineSegment(sketch, "E204.0", {"start": v(-67.55, 7.5) * mm, "end": v(65.89, 7.5) * mm});
            skLineSegment(sketch, "E205.0", {"start": v(-67.55, -7.5) * mm, "end": v(65.89, -7.5) * mm});
            skLineSegment(sketch, "E206.0", {"start": v(-67.55, 8.75) * mm, "end": v(65.89, 8.75) * mm});
            skPoint(sketch, "E207.0", {"position": v(-21, 0) * mm});
            skLineSegment(sketch, "E208", {"start": v(-21, 0) * mm, "end": v(-21, 16.06) * mm});
            skLineSegment(sketch, "E209.0", {"start": v(-16.2, 0) * mm, "end": v(-16.2, 16.06) * mm});
            skFitSpline(sketch, "E210", {"points": [v(-16.2, 7.5) * mm, v(12.04, 8) * mm, v(35.8, 8.9) * mm], "startDerivative": vector(77.6, 0.2) * mm, "endDerivative": vector(15.7, 2.89) * mm});
            skLineSegment(sketch, "E211", {"start": v(-16.2, 16.06) * mm, "end": v(35.8, 16.06) * mm});
            skLineSegment(sketch, "E212", {"start": v(35.8, 16.06) * mm, "end": v(35.8, 8.9) * mm});
            skLineSegment(sketch, "E213.MirrorCS", {"start": v(-16.2, 0) * mm, "end": v(-16.2, -16.06) * mm});
            skLineSegment(sketch, "E214.MirrorCS", {"start": v(-16.2, -16.06) * mm, "end": v(35.8, -16.06) * mm});
            skLineSegment(sketch, "E215.MirrorCS", {"start": v(35.8, -16.06) * mm, "end": v(35.8, -8.9) * mm});
            skFitSpline(sketch, "E216.MirrorCS", {"points": [v(-16.2, -7.5) * mm, v(12.04, -8) * mm, v(35.8, -8.9) * mm], "startDerivative": vector(77.6, -0.2) * mm, "endDerivative": vector(15.7, -2.89) * mm});
            skSolve(sketch);
        }
        {
            var Q0;
            {var subQ6=sQuery(id+"F24.wireOp",EDGE,"E211");Q0=makeQuery(id+"F24.imprint","IMPRINT",FACE,{"disambiguationData":[TD([[makeQuery(id+"F24.imprint","IMPRINT",EDGE,{"derivedFrom":subQ6}),-1.0]])]});}
            var Q1;
            {var subQ0=sQuery(id+"F24.wireOp",EDGE,"E214.MirrorCS");Q1=makeQuery(id+"F24.imprint","IMPRINT",FACE,{"disambiguationData":[TD([[makeQuery(id+"F24.imprint","IMPRINT",EDGE,{"derivedFrom":subQ0}),1.0]])]});}
            extrude(context, id + "F25", {"entities" : qUnion([Q0, Q1]), "operationType" : NewBodyOperationType.REMOVE, "endBound" : BoundingType.THROUGH_ALL, "depth" : 25 * mm});
        }
        {
            var Q0;
            Q0=makeQuery(id+"F21.imprint","IMPRINT",FACE,{"disambiguationData":[TD([[makeQuery(id+"F21.imprint","IMPRINT",EDGE,{"derivedFrom":sQuery(id+"F21.wireOp",EDGE,"E186")}),-1.0]])]});
            extrude(context, id + "F26", {"entities" : qUnion([Q0]), "operationType" : NewBodyOperationType.REMOVE, "endBound" : BoundingType.SYMMETRIC, "oppositeDirection" : true, "depth" : 25 * mm});
        }
        {
            var Q0;
            Q0=makeQuery(id+"F26.boolean.opBoolean","COPY",FACE,{"derivedFrom":makeQuery(id+"F26.opExtrude","SWEPT_FACE",FACE,{"disambiguationData":[OSD([sQuery(id+"F21.wireOp",EDGE,"E186")])]})});
            cPlane(context, id + "F27", {"entities" : qUnion([Q0]), "cplaneType" : CPlaneType.OFFSET, "offset" : 13 * mm, "oppositeDirection" : true, "width" : 150 * mm, "height" : 150 * mm});
        }
    });
